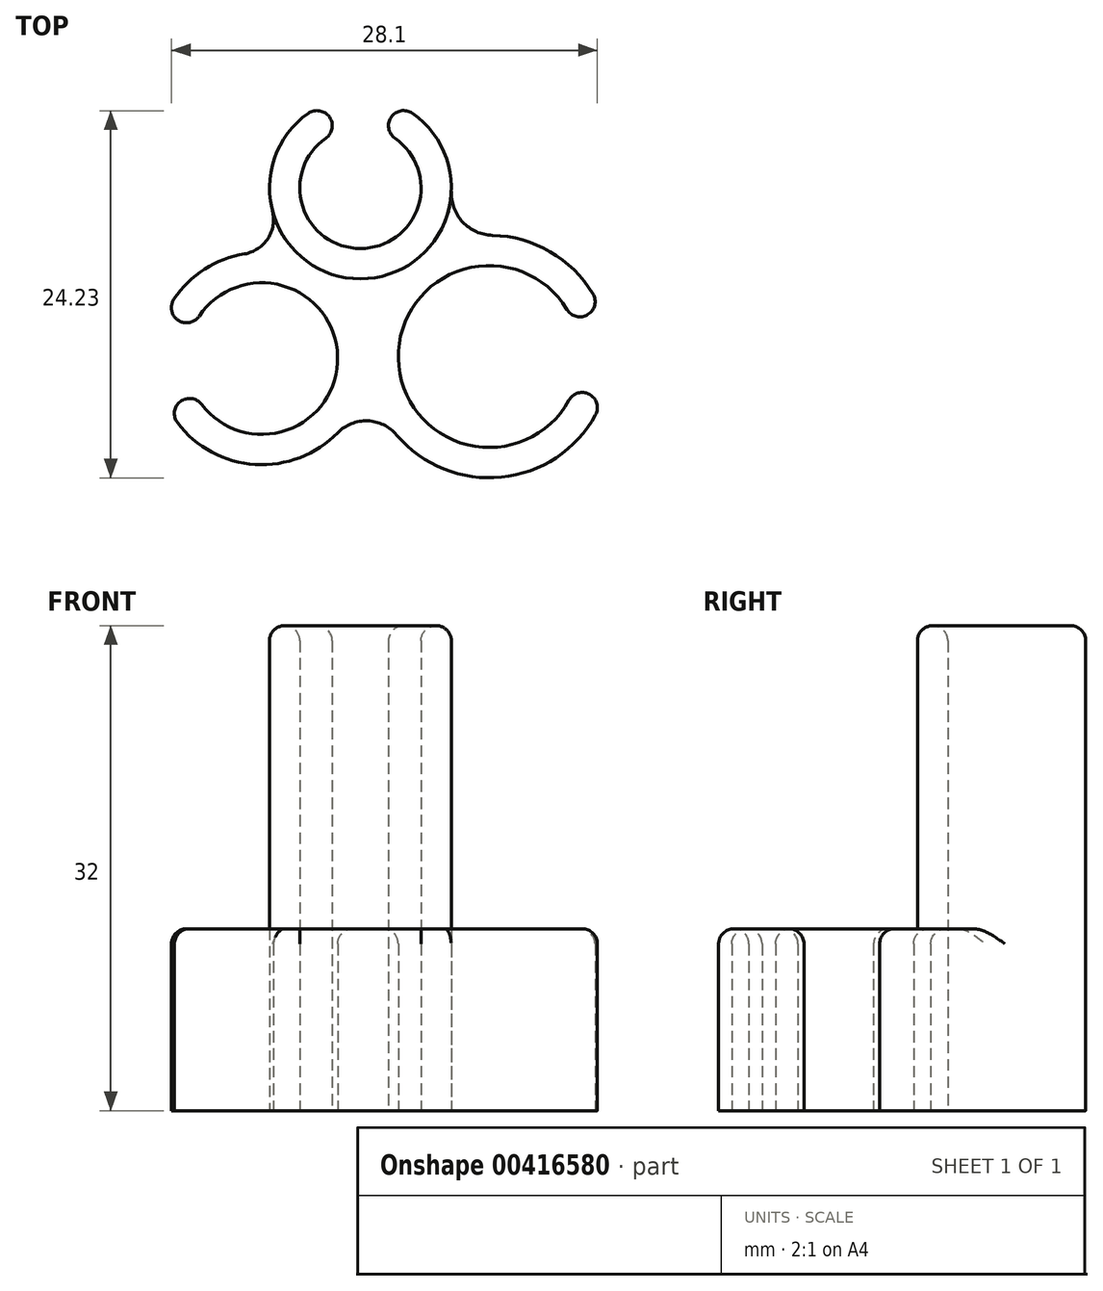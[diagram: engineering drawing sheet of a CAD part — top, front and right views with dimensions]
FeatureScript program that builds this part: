
annotation { "Feature Type Name" : "Feature", "Feature Type Description" : "" }
export const myFeature = defineFeature(function(context is Context, id is Id, definition is map)
    precondition{}
    {
        {
            var Q0;
            Q0=qCreatedBy(makeId("Top.planeOp"),FACE);
            var sketch = newSketch(context, id + "F0", { "sketchPlane" : qUnion([Q0])});
            skArc(sketch, "E0", {"start": v(-6.8, -8.16) * mm, "mid": v(-10.15, -9.7) * mm, "end": v(-12.25, -12.73) * mm});
            skArc(sketch, "E1", {"start": v(3.25, -20.1) * mm, "mid": v(10.96, -22.77) * mm, "end": v(17, -17.28) * mm});
            skArc(sketch, "E2", {"start": v(6.84, -4.04) * mm, "mid": v(5.77, -0.38) * mm, "end": v(2.7, 1.9) * mm});
            skArc(sketch, "E3", {"start": v(14.75, -12.32) * mm, "mid": v(3.35, -15.07) * mm, "end": v(14.86, -17.31) * mm});
            skArc(sketch, "E4", {"start": v(-1.01, -0.27) * mm, "mid": v(0.85, -7.81) * mm, "end": v(2.7, -0.27) * mm});
            skArc(sketch, "E5", {"start": v(-9.9, -17.7) * mm, "mid": v(-0.65, -14.92) * mm, "end": v(-10.06, -12.7) * mm});
            skArc(sketch, "E6", {"start": v(6.84, -4.04) * mm, "mid": v(7.6, -6.06) * mm, "end": v(9.56, -6.94) * mm});
            skArc(sketch, "E7", {"start": v(3.25, -20.1) * mm, "mid": v(1.33, -19.18) * mm, "end": v(-0.65, -19.97) * mm});
            skArc(sketch, "E8", {"start": v(-6.8, -8.16) * mm, "mid": v(-5.25, -7.15) * mm, "end": v(-4.96, -5.32) * mm});
            skLineSegment(sketch, "E9", {"start": v(16.9, -12.29) * mm, "end": v(14.75, -12.32) * mm});
            skLineSegment(sketch, "E10", {"start": v(-12.13, -17.73) * mm, "end": v(-9.9, -17.7) * mm});
            skArc(sketch, "E11.trimOffspring", {"start": v(16.9, -12.29) * mm, "mid": v(14.06, -8.47) * mm, "end": v(9.56, -6.94) * mm});
            skArc(sketch, "E12.trimOffspring", {"start": v(-12.13, -17.73) * mm, "mid": v(-7, -21.94) * mm, "end": v(-0.65, -19.97) * mm});
            skPoint(sketch, "E13.start.orphan", {"position": v(20.68, -17.22) * mm});
            skPoint(sketch, "E14.orphan", {"position": v(20.33, -12.23) * mm});
            skLineSegment(sketch, "E15.trimOffspring", {"start": v(-10.06, -12.7) * mm, "end": v(-12.25, -12.73) * mm});
            skLineSegment(sketch, "E16.trimOffspring", {"start": v(14.86, -17.31) * mm, "end": v(17, -17.28) * mm});
            skLineSegment(sketch, "E17.left", {"start": v(-1.01, 1.9) * mm, "end": v(-1.01, -0.27) * mm});
            skLineSegment(sketch, "E17.right", {"start": v(2.7, 1.9) * mm, "end": v(2.7, -0.27) * mm});
            skArc(sketch, "E18.trimOffspring", {"start": v(-1.01, 1.9) * mm, "mid": v(-4.42, -0.93) * mm, "end": v(-4.96, -5.32) * mm});
            skPoint(sketch, "E17.top.end.orphan", {"position": v(2.7, -3.81) * mm});
            skPoint(sketch, "E19.orphan", {"position": v(-1.01, 3.52) * mm});
            skPoint(sketch, "E20.orphan", {"position": v(2.7, 3.52) * mm});
            skSolve(sketch);
        }
        {
            var Q0;
            Q0 = qSketchRegion(id + "F0", true);
            extrude(context, id + "F1", {"entities" : qUnion([Q0]), "depth" : 12 * mm});
        }
        {
            var Q0;
            Q0=makeQuery(id+"F1.opExtrude","CAP_FACE",FACE,{"disambiguationData":[OSD([sQuery(id+"F0.wireOp",EDGE,"E0"),sQuery(id+"F0.wireOp",EDGE,"E1"),sQuery(id+"F0.wireOp",EDGE,"E2"),sQuery(id+"F0.wireOp",EDGE,"E3"),sQuery(id+"F0.wireOp",EDGE,"E4"),sQuery(id+"F0.wireOp",EDGE,"E5"),sQuery(id+"F0.wireOp",EDGE,"E6"),sQuery(id+"F0.wireOp",EDGE,"E7"),sQuery(id+"F0.wireOp",EDGE,"E8"),sQuery(id+"F0.wireOp",EDGE,"E9"),sQuery(id+"F0.wireOp",EDGE,"E10"),sQuery(id+"F0.wireOp",EDGE,"E11.trimOffspring"),sQuery(id+"F0.wireOp",EDGE,"E12.trimOffspring"),sQuery(id+"F0.wireOp",EDGE,"E15.trimOffspring"),sQuery(id+"F0.wireOp",EDGE,"E16.trimOffspring"),sQuery(id+"F0.wireOp",EDGE,"E17.left"),sQuery(id+"F0.wireOp",EDGE,"E17.right"),sQuery(id+"F0.wireOp",EDGE,"E18.trimOffspring")])],"isStart":false});
            var sketch = newSketch(context, id + "F2", { "sketchPlane" : qUnion([Q0])});
            skArc(sketch, "E21", {"start": v(-1.01, 1.9) * mm, "mid": v(0.85, -9.81) * mm, "end": v(2.7, 1.9) * mm});
            skArc(sketch, "E22", {"start": v(-1.01, -0.27) * mm, "mid": v(0.85, -7.81) * mm, "end": v(2.7, -0.27) * mm});
            skLineSegment(sketch, "E23", {"start": v(-1.01, -0.27) * mm, "end": v(-1.01, 1.9) * mm});
            skLineSegment(sketch, "E24", {"start": v(2.7, -0.27) * mm, "end": v(2.7, 1.9) * mm});
            skSolve(sketch);
        }
        {
            var Q0;
            Q0=makeQuery(id+"F2.imprint","IMPRINT",FACE,{"disambiguationData":[TD([[makeQuery(id+"F2.imprint","IMPRINT",EDGE,{"derivedFrom":sQuery(id+"F2.wireOp",EDGE,"E22")}),-1.0]])]});
            extrude(context, id + "F3", {"entities" : qUnion([Q0]), "operationType" : NewBodyOperationType.ADD, "depth" : 20 * mm});
        }
        {
            var Q0;
            Q0=makeQuery(id+"F3.boolean.opBoolean","MERGE",EDGE,{"derivedFrom":[makeQuery(id+"F1.opExtrude","SWEPT_EDGE",EDGE,{"disambiguationData":[OSD([sQuery(id+"F0.wireOp",EDGE,"E2"),sQuery(id+"F0.wireOp",EDGE,"E17.right")])]}),makeQuery(id+"F3.opExtrude","SWEPT_EDGE",EDGE,{"disambiguationData":[OSD([sQuery(id+"F2.wireOp",EDGE,"E21"),sQuery(id+"F2.wireOp",EDGE,"E24")])]})]});
            var Q1;
            Q1=makeQuery(id+"F3.boolean.opBoolean","MERGE",EDGE,{"derivedFrom":[makeQuery(id+"F1.opExtrude","SWEPT_EDGE",EDGE,{"disambiguationData":[OSD([sQuery(id+"F0.wireOp",EDGE,"E17.left"),sQuery(id+"F0.wireOp",EDGE,"E18.trimOffspring")])]}),makeQuery(id+"F3.opExtrude","SWEPT_EDGE",EDGE,{"disambiguationData":[OSD([sQuery(id+"F2.wireOp",EDGE,"E21"),sQuery(id+"F2.wireOp",EDGE,"E23")])]})]});
            var Q2;
            Q2=makeQuery(id+"F1.opExtrude","SWEPT_EDGE",EDGE,{"disambiguationData":[OSD([sQuery(id+"F0.wireOp",EDGE,"E10"),sQuery(id+"F0.wireOp",EDGE,"E12.trimOffspring")])]});
            var Q3;
            Q3=makeQuery(id+"F1.opExtrude","SWEPT_EDGE",EDGE,{"disambiguationData":[OSD([sQuery(id+"F0.wireOp",EDGE,"E0"),sQuery(id+"F0.wireOp",EDGE,"E15.trimOffspring")])]});
            fillet(context, id + "F4", {"entities" : qUnion([Q0, Q1, Q2, Q3]), "radius" : 1 * mm, "tangentPropagation" : true, "allowEdgeOverflow" : false});
        }
        {
            var Q0;
            Q0=makeQuery(id+"F3.boolean.opBoolean","MERGE",EDGE,{"derivedFrom":[makeQuery(id+"F1.opExtrude","SWEPT_EDGE",EDGE,{"disambiguationData":[OSD([sQuery(id+"F0.wireOp",EDGE,"E4"),sQuery(id+"F0.wireOp",EDGE,"E17.left")])]}),makeQuery(id+"F3.opExtrude","SWEPT_EDGE",EDGE,{"disambiguationData":[OSD([sQuery(id+"F2.wireOp",EDGE,"E22"),sQuery(id+"F2.wireOp",EDGE,"E23")])]})]});
            var Q1;
            Q1=makeQuery(id+"F1.opExtrude","SWEPT_EDGE",EDGE,{"disambiguationData":[OSD([sQuery(id+"F0.wireOp",EDGE,"E5"),sQuery(id+"F0.wireOp",EDGE,"E15.trimOffspring")])]});
            var Q2;
            Q2=makeQuery(id+"F1.opExtrude","SWEPT_EDGE",EDGE,{"disambiguationData":[OSD([sQuery(id+"F0.wireOp",EDGE,"E5"),sQuery(id+"F0.wireOp",EDGE,"E10")])]});
            fillet(context, id + "F5", {"entities" : qUnion([Q0, Q1, Q2]), "radius" : 1 * mm, "tangentPropagation" : true, "allowEdgeOverflow" : false});
        }
        {
            var Q0;
            Q0=makeQuery(id+"F3.boolean.opBoolean","MERGE",EDGE,{"derivedFrom":[makeQuery(id+"F1.opExtrude","SWEPT_EDGE",EDGE,{"disambiguationData":[OSD([sQuery(id+"F0.wireOp",EDGE,"E4"),sQuery(id+"F0.wireOp",EDGE,"E17.right")])]}),makeQuery(id+"F3.opExtrude","SWEPT_EDGE",EDGE,{"disambiguationData":[OSD([sQuery(id+"F2.wireOp",EDGE,"E22"),sQuery(id+"F2.wireOp",EDGE,"E24")])]})]});
            fillet(context, id + "F6", {"entities" : qUnion([Q0]), "radius" : 1 * mm, "tangentPropagation" : true, "allowEdgeOverflow" : false});
        }
        {
            var Q0;
            Q0=makeQuery(id+"F1.opExtrude","SWEPT_EDGE",EDGE,{"disambiguationData":[OSD([sQuery(id+"F0.wireOp",EDGE,"E1"),sQuery(id+"F0.wireOp",EDGE,"E16.trimOffspring")])]});
            var Q1;
            Q1=makeQuery(id+"F1.opExtrude","SWEPT_EDGE",EDGE,{"disambiguationData":[OSD([sQuery(id+"F0.wireOp",EDGE,"E9"),sQuery(id+"F0.wireOp",EDGE,"E11.trimOffspring")])]});
            var Q2;
            Q2=makeQuery(id+"F1.opExtrude","SWEPT_EDGE",EDGE,{"disambiguationData":[OSD([sQuery(id+"F0.wireOp",EDGE,"E3"),sQuery(id+"F0.wireOp",EDGE,"E9")])]});
            var Q3;
            Q3=makeQuery(id+"F1.opExtrude","SWEPT_EDGE",EDGE,{"disambiguationData":[OSD([sQuery(id+"F0.wireOp",EDGE,"E3"),sQuery(id+"F0.wireOp",EDGE,"E16.trimOffspring")])]});
            fillet(context, id + "F7", {"entities" : qUnion([Q0, Q1, Q2, Q3]), "radius" : 1 * mm, "tangentPropagation" : true, "allowEdgeOverflow" : false});
        }
        {
            var Q0;
            Q0=makeQuery(id+"F1.opExtrude","CAP_EDGE",EDGE,{"disambiguationData":[OSD([sQuery(id+"F0.wireOp",EDGE,"E3")])],"isStart":false});
            var Q1;
            Q1=makeQuery(id+"F1.opExtrude","CAP_EDGE",EDGE,{"disambiguationData":[OSD([sQuery(id+"F0.wireOp",EDGE,"E5")])],"isStart":false});
            var Q2;
            Q2=makeQuery(id+"F3.opExtrude","CAP_EDGE",EDGE,{"disambiguationData":[OSD([sQuery(id+"F2.wireOp",EDGE,"E22")])],"isStart":false});
            fillet(context, id + "F8", {"entities" : qUnion([Q0, Q1, Q2]), "radius" : 1 * mm, "tangentPropagation" : true, "allowEdgeOverflow" : false});
        }
    });
